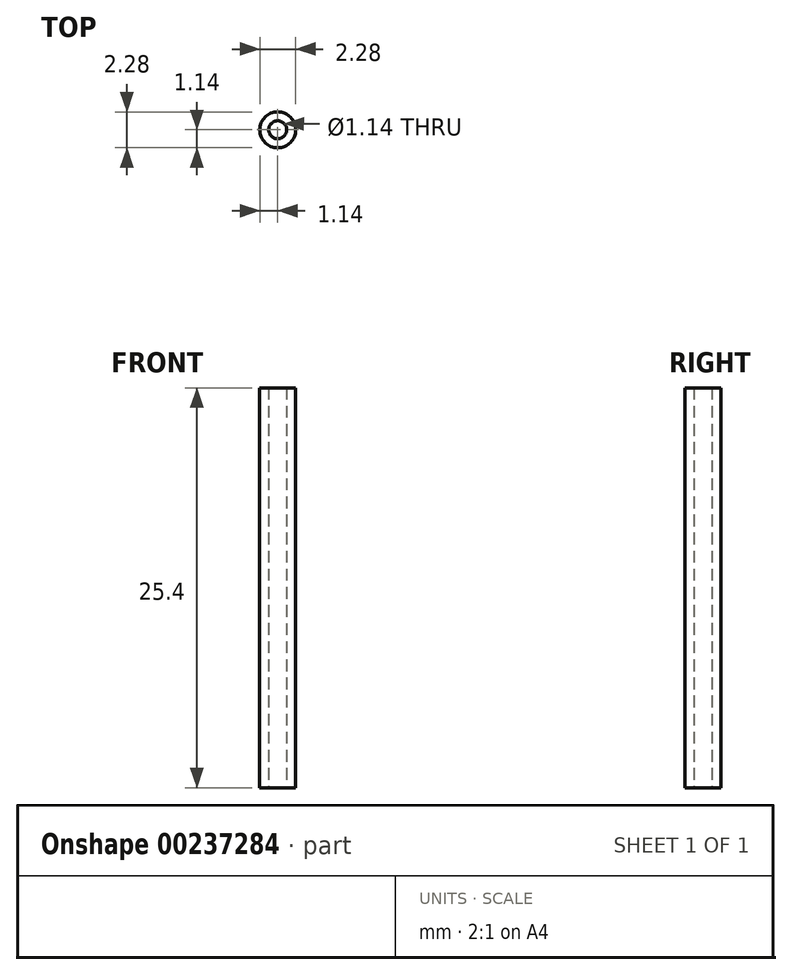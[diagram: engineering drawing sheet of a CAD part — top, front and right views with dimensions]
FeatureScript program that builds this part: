
annotation { "Feature Type Name" : "Feature", "Feature Type Description" : "" }
export const myFeature = defineFeature(function(context is Context, id is Id, definition is map)
    precondition{}
    {
        {
            var Q0;
            Q0=qCreatedBy(makeId("Top.planeOp"),FACE);
            var sketch = newSketch(context, id + "F0", { "sketchPlane" : qUnion([Q0])});
            skCircle(sketch, "E0", {"center": v(0, 0) * mm, "radius": 1.14 * mm});
            skCircle(sketch, "E1", {"center": v(0, 0) * mm, "radius": 0.57 * mm});
            skSolve(sketch);
        }
        {
            var Q0;
            Q0=makeQuery(id+"F0.imprint","IMPRINT",FACE,{"disambiguationData":[TD([[makeQuery(id+"F0.imprint","IMPRINT",EDGE,{"derivedFrom":sQuery(id+"F0.wireOp",EDGE,"E0")}),1.0]])]});
            extrude(context, id + "F1", {"entities" : qUnion([Q0]), "depth" : 25.4 * mm});
        }
    });
